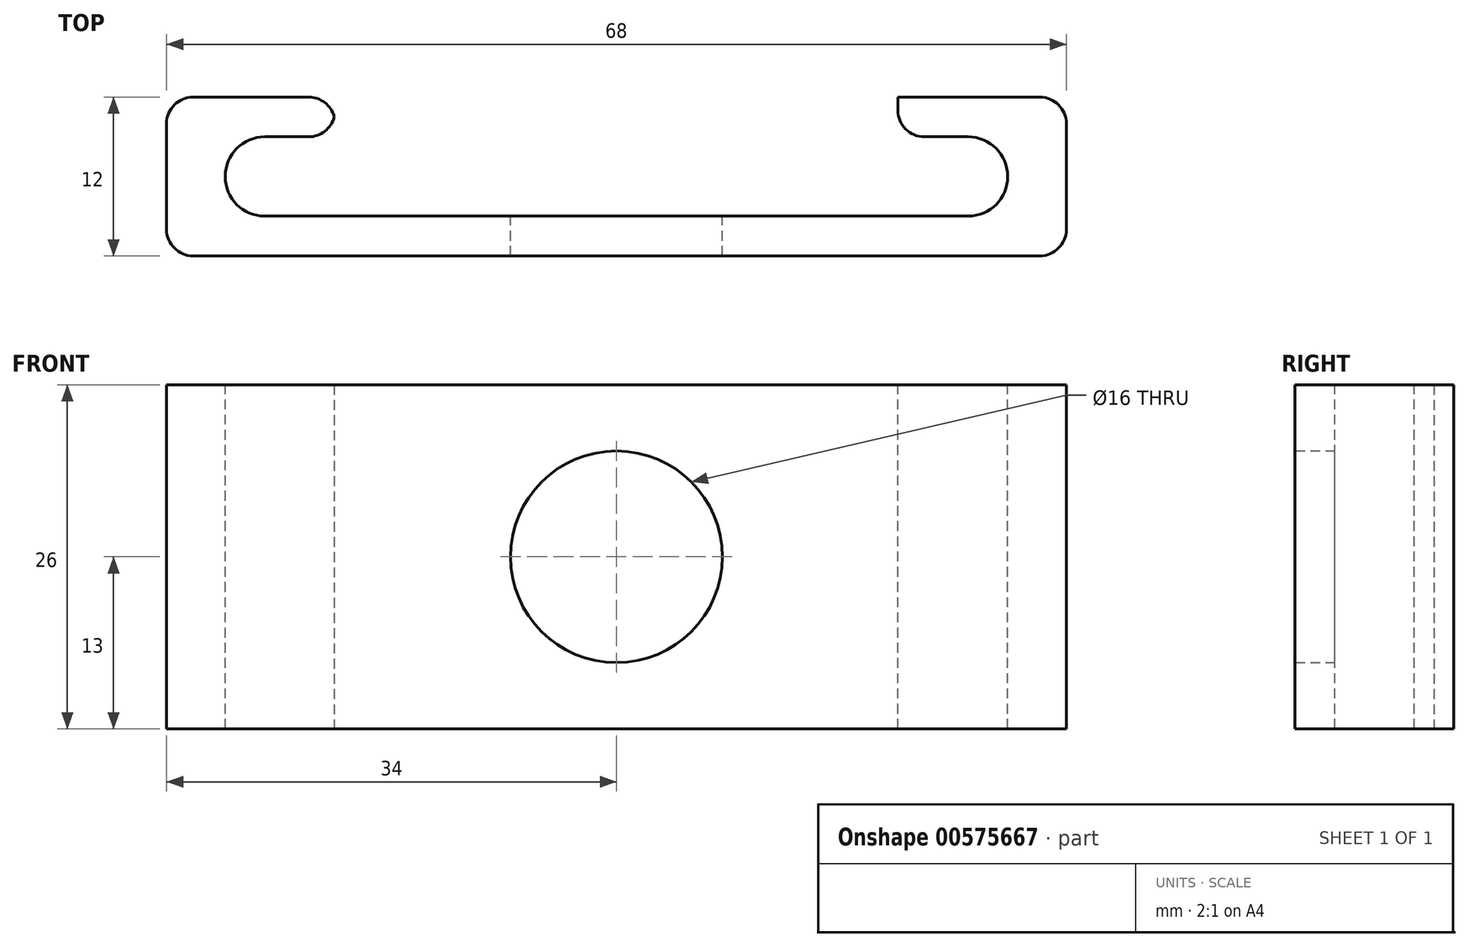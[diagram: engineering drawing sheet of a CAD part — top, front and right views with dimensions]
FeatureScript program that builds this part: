
annotation { "Feature Type Name" : "Feature", "Feature Type Description" : "" }
export const myFeature = defineFeature(function(context is Context, id is Id, definition is map)
    precondition{}
    {
        {
            var Q0;
            Q0=qCreatedBy(makeId("Front.planeOp"),FACE);
            var sketch = newSketch(context, id + "F0", { "sketchPlane" : qUnion([Q0])});
            skLineSegment(sketch, "E0.bottom", {"start": v(-34, 13) * mm, "end": v(34, 13) * mm});
            skLineSegment(sketch, "E0.top", {"start": v(-34, -13) * mm, "end": v(34, -13) * mm});
            skLineSegment(sketch, "E0.left", {"start": v(-34, 13) * mm, "end": v(-34, -13) * mm});
            skLineSegment(sketch, "E0.right", {"start": v(34, 13) * mm, "end": v(34, -13) * mm});
            skPoint(sketch, "E0.middle", {"position": v(0, 0) * mm});
            skCircle(sketch, "E1", {"center": v(0, 0) * mm, "radius": 8 * mm});
            skLineSegment(sketch, "E2", {"start": v(-34, 0) * mm, "end": v(-31, 0) * mm});
            skPoint(sketch, "E2.endSnap0", {"position": v(-34, 0) * mm});
            skSolve(sketch);
        }
        {
            var Q0;
            Q0=makeQuery(id+"F0.imprint","IMPRINT",FACE,{"disambiguationData":[TD([[makeQuery(id+"F0.imprint","IMPRINT",EDGE,{"derivedFrom":sQuery(id+"F0.wireOp",EDGE,"E0.bottom")}),-1.0]])]});
            extrude(context, id + "F1", {"entities" : qUnion([Q0]), "depth" : 12 * mm, "offsetDistance" : 25 * mm});
        }
        {
            var Q0;
            Q0=makeQuery(id+"F1.opExtrude","SWEPT_FACE",FACE,{"disambiguationData":[OSD([sQuery(id+"F0.wireOp",EDGE,"E0.bottom")])]});
            var sketch = newSketch(context, id + "F2", { "sketchPlane" : qUnion([Q0])});
            skLineSegment(sketch, "E3.bottom", {"start": v(-26.57, -3) * mm, "end": v(-21.27, -3) * mm});
            skLineSegment(sketch, "E3.top", {"start": v(-26.57, -9) * mm, "end": v(26.57, -9) * mm});
            skLineSegment(sketch, "E3.left", {"start": v(-29.57, -6) * mm, "end": v(-29.57, -6) * mm});
            skLineSegment(sketch, "E3.right", {"start": v(29.57, -6) * mm, "end": v(29.57, -6) * mm});
            skPoint(sketch, "E3.middle", {"position": v(0, -6) * mm});
            skLineSegment(sketch, "E4", {"start": v(-21.27, -3) * mm, "end": v(-21.27, 0) * mm});
            skLineSegment(sketch, "E5", {"start": v(21.27, 0) * mm, "end": v(21.27, -3) * mm});
            skLineSegment(sketch, "E6", {"start": v(-21.27, 0) * mm, "end": v(0, 0) * mm});
            skLineSegment(sketch, "E7", {"start": v(21.27, 0) * mm, "end": v(0, 0) * mm});
            skPoint(sketch, "E8.visualSharp", {"position": v(-29.57, -9) * mm});
            skArc(sketch, "E8.filletArc", {"start": v(-29.57, -6) * mm, "mid": v(-28.7, -8.12) * mm, "end": v(-26.57, -9) * mm});
            skPoint(sketch, "E9.visualSharp", {"position": v(-29.57, -3) * mm});
            skArc(sketch, "E9.filletArc", {"start": v(-26.57, -3) * mm, "mid": v(-28.7, -3.88) * mm, "end": v(-29.57, -6) * mm});
            skPoint(sketch, "E10.visualSharp", {"position": v(29.57, -9) * mm});
            skArc(sketch, "E10.filletArc", {"start": v(26.57, -9) * mm, "mid": v(28.7, -8.12) * mm, "end": v(29.57, -6) * mm});
            skPoint(sketch, "E11.visualSharp", {"position": v(29.57, -3) * mm});
            skArc(sketch, "E11.filletArc", {"start": v(29.57, -6) * mm, "mid": v(28.7, -3.88) * mm, "end": v(26.57, -3) * mm});
            skLineSegment(sketch, "E12.trimOffspring", {"start": v(21.27, -3) * mm, "end": v(26.57, -3) * mm});
            skSolve(sketch);
        }
        {
            var Q0;
            {var subQ0=sQuery(id+"F2.wireOp",EDGE,"E3.left");Q0=makeQuery(id+"F2.imprint","IMPRINT",FACE,{"disambiguationData":[TD([[makeQuery(id+"F2.imprint","IMPRINT",EDGE,{"derivedFrom":subQ0}),1.0]])]});}
            var Q1;
            {var subQ0=sQuery(id+"F2.wireOp",EDGE,"E3.right");Q1=makeQuery(id+"F2.imprint","IMPRINT",FACE,{"disambiguationData":[TD([[makeQuery(id+"F2.imprint","IMPRINT",EDGE,{"derivedFrom":subQ0}),-1.0]])]});}
            var Q2;
            {var subQ4=sQuery(id+"F2.wireOp",EDGE,"E5");Q2=makeQuery(id+"F2.imprint","IMPRINT",FACE,{"disambiguationData":[TD([[makeQuery(id+"F2.imprint","IMPRINT",EDGE,{"derivedFrom":subQ4}),-1.0]])]});}
            var Q3;
            {var subQ4=sQuery(id+"F2.wireOp",EDGE,"E4");Q3=makeQuery(id+"F2.imprint","IMPRINT",FACE,{"disambiguationData":[TD([[makeQuery(id+"F2.imprint","IMPRINT",EDGE,{"derivedFrom":subQ4}),-1.0]])]});}
            extrude(context, id + "F3", {"entities" : qUnion([Q0, Q1, Q2, Q3]), "operationType" : NewBodyOperationType.REMOVE, "oppositeDirection" : true, "depth" : 40 * mm, "offsetDistance" : 25 * mm});
        }
        {
            var Q0;
            Q0=makeQuery(id+"F1.opExtrude","CAP_EDGE",EDGE,{"disambiguationData":[OSD([sQuery(id+"F0.wireOp",EDGE,"E0.right")])],"isStart":false});
            var Q1;
            Q1=makeQuery(id+"F1.opExtrude","CAP_EDGE",EDGE,{"disambiguationData":[OSD([sQuery(id+"F0.wireOp",EDGE,"E0.right")])],"isStart":true});
            var Q2;
            Q2=makeQuery(id+"F3.boolean.opBoolean","COPY",EDGE,{"derivedFrom":makeQuery(id+"F3.opExtrude","SWEPT_EDGE",EDGE,{"disambiguationData":[OSD([sQuery(id+"F0.wireOp",EDGE,"E0.bottom"),sQuery(id+"F2.wireOp",EDGE,"E4"),sQuery(id+"F2.wireOp",EDGE,"E6")])]})});
            var Q3;
            Q3=makeQuery(id+"F3.boolean.opBoolean","COPY",EDGE,{"derivedFrom":makeQuery(id+"F3.opExtrude","SWEPT_EDGE",EDGE,{"disambiguationData":[OSD([sQuery(id+"F0.wireOp",EDGE,"E0.bottom"),sQuery(id+"F2.wireOp",EDGE,"E5"),sQuery(id+"F2.wireOp",EDGE,"E7")])]})});
            var Q4;
            Q4=makeQuery(id+"F1.opExtrude","CAP_EDGE",EDGE,{"disambiguationData":[OSD([sQuery(id+"F0.wireOp",EDGE,"E0.left")])],"isStart":true});
            var Q5;
            Q5=makeQuery(id+"F1.opExtrude","CAP_EDGE",EDGE,{"disambiguationData":[OSD([sQuery(id+"F0.wireOp",EDGE,"E0.left")])],"isStart":false});
            var Q6;
            Q6=makeQuery(id+"F3.boolean.opBoolean","COPY",EDGE,{"derivedFrom":makeQuery(id+"F3.opExtrude","SWEPT_EDGE",EDGE,{"disambiguationData":[OSD([sQuery(id+"F2.wireOp",EDGE,"E3.bottom"),sQuery(id+"F2.wireOp",EDGE,"E4")])]})});
            var Q7;
            Q7=makeQuery(id+"F3.boolean.opBoolean","COPY",EDGE,{"derivedFrom":makeQuery(id+"F3.opExtrude","SWEPT_EDGE",EDGE,{"disambiguationData":[OSD([sQuery(id+"F2.wireOp",EDGE,"E5"),sQuery(id+"F2.wireOp",EDGE,"E12.trimOffspring")])]})});
            fillet(context, id + "F4", {"entities" : qUnion([Q0, Q1, Q2, Q3, Q4, Q5, Q6, Q7]), "radius" : 2 * mm, "tangentPropagation" : true, "allowEdgeOverflow" : false});
        }
    });
